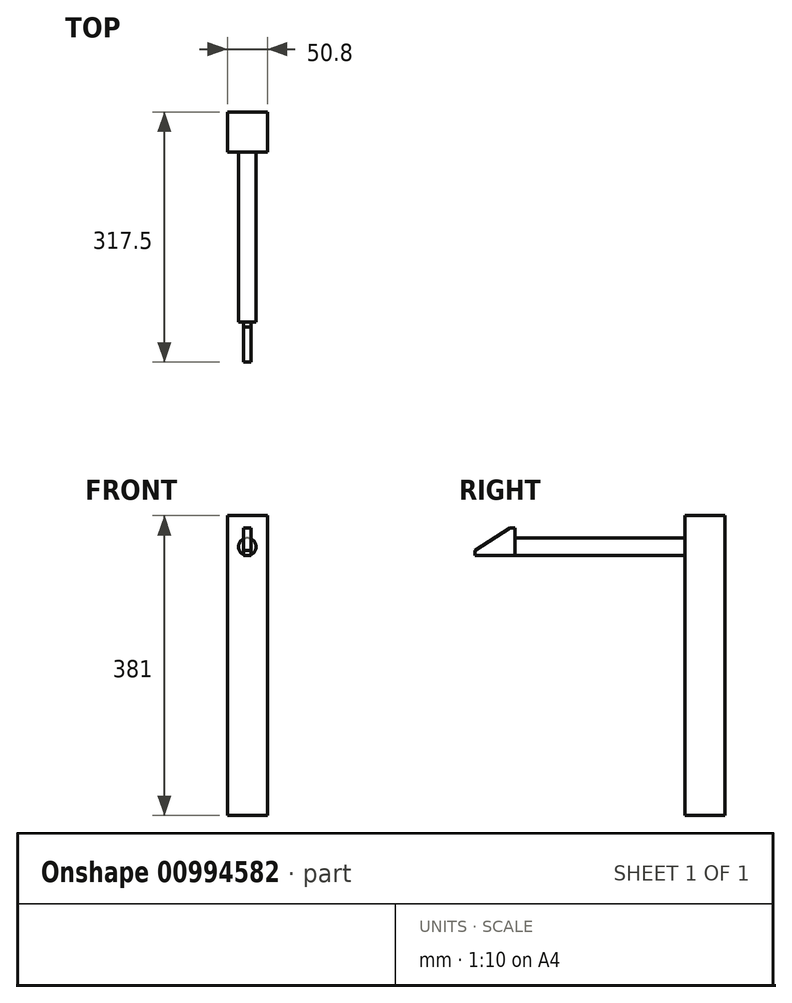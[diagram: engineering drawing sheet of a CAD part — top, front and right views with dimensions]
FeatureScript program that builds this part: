
annotation { "Feature Type Name" : "Feature", "Feature Type Description" : "" }
export const myFeature = defineFeature(function(context is Context, id is Id, definition is map)
    precondition{}
    {
        {
            var Q0;
            Q0=qCreatedBy(makeId("Top.planeOp"),FACE);
            var sketch = newSketch(context, id + "F0", { "sketchPlane" : qUnion([Q0])});
            skLineSegment(sketch, "E0.bottom", {"start": v(25.4, -25.4) * mm, "end": v(-25.4, -25.4) * mm});
            skLineSegment(sketch, "E0.top", {"start": v(25.4, 25.4) * mm, "end": v(-25.4, 25.4) * mm});
            skLineSegment(sketch, "E0.left", {"start": v(25.4, -25.4) * mm, "end": v(25.4, 25.4) * mm});
            skLineSegment(sketch, "E0.right", {"start": v(-25.4, -25.4) * mm, "end": v(-25.4, 25.4) * mm});
            skPoint(sketch, "E0.middle", {"position": v(0, 0) * mm});
            skSolve(sketch);
        }
        {
            var Q0;
            Q0=makeQuery(id+"F0.imprint","IMPRINT",FACE,{"disambiguationData":[TD([[makeQuery(id+"F0.imprint","IMPRINT",EDGE,{"derivedFrom":sQuery(id+"F0.wireOp",EDGE,"E0.bottom")}),-1.0]])]});
            extrude(context, id + "F1", {"entities" : qUnion([Q0]), "depth" : 381 * mm, "offsetDistance" : 25.4 * mm});
        }
        {
            var Q0;
            Q0=makeQuery(id+"F1.opExtrude","SWEPT_FACE",FACE,{"disambiguationData":[OSD([sQuery(id+"F0.wireOp",EDGE,"E0.bottom")])]});
            var sketch = newSketch(context, id + "F2", { "sketchPlane" : qUnion([Q0])});
            skCircle(sketch, "E1", {"center": v(0, 341.31) * mm, "radius": 11.11 * mm});
            skSolve(sketch);
        }
        {
            var Q0;
            Q0=makeQuery(id+"F2.imprint","IMPRINT",FACE,{"disambiguationData":[TD([[makeQuery(id+"F2.imprint","IMPRINT",EDGE,{"derivedFrom":sQuery(id+"F2.wireOp",EDGE,"E1")}),1.0]])]});
            extrude(context, id + "F3", {"entities" : qUnion([Q0]), "operationType" : NewBodyOperationType.ADD, "depth" : 215.9 * mm, "offsetDistance" : 25.4 * mm});
        }
        {
            var Q0;
            Q0=qCreatedBy(makeId("Right.planeOp"),FACE);
            var sketch = newSketch(context, id + "F4", { "sketchPlane" : qUnion([Q0])});
            skLineSegment(sketch, "E2", {"start": v(-241.3, 330.2) * mm, "end": v(-241.3, 365.13) * mm});
            skLineSegment(sketch, "E3", {"start": v(-247.65, 365.13) * mm, "end": v(-292.1, 336.55) * mm});
            skLineSegment(sketch, "E4", {"start": v(-292.1, 336.55) * mm, "end": v(-292.1, 330.2) * mm});
            skLineSegment(sketch, "E5", {"start": v(-292.1, 330.2) * mm, "end": v(-241.3, 330.2) * mm});
            skLineSegment(sketch, "E6", {"start": v(-241.3, 365.13) * mm, "end": v(-247.65, 365.13) * mm});
            skSolve(sketch);
        }
        {
            var Q0;
            Q0 = qSketchRegion(id + "F4", true);
            extrude(context, id + "F5", {"entities" : qUnion([Q0]), "operationType" : NewBodyOperationType.ADD, "depth" : 4.76 * mm, "offsetDistance" : 25.4 * mm, "hasSecondDirection" : true, "secondDirectionOppositeDirection" : true, "secondDirectionDepth" : 4.76 * mm});
        }
        {
            var Q0;
            Q0=qCreatedBy(makeId("Front.planeOp"),FACE);
            var sketch = newSketch(context, id + "F6", { "sketchPlane" : qUnion([Q0])});
            skLineSegment(sketch, "E7", {"start": v(-635, 0) * mm, "end": v(635, 0) * mm});
            skSolve(sketch);
        }
        {
            var Q0;
            Q0=sQuery(id+"F6.wireOp",EDGE,"E7");
            extrude(context, id + "F7", {"bodyType" : ToolBodyType.SURFACE, "surfaceEntities" : qUnion([Q0]), "depth" : 635 * mm, "offsetDistance" : 25.4 * mm, "hasSecondDirection" : true, "secondDirectionOppositeDirection" : true, "secondDirectionDepth" : 635 * mm});
        }
    });
